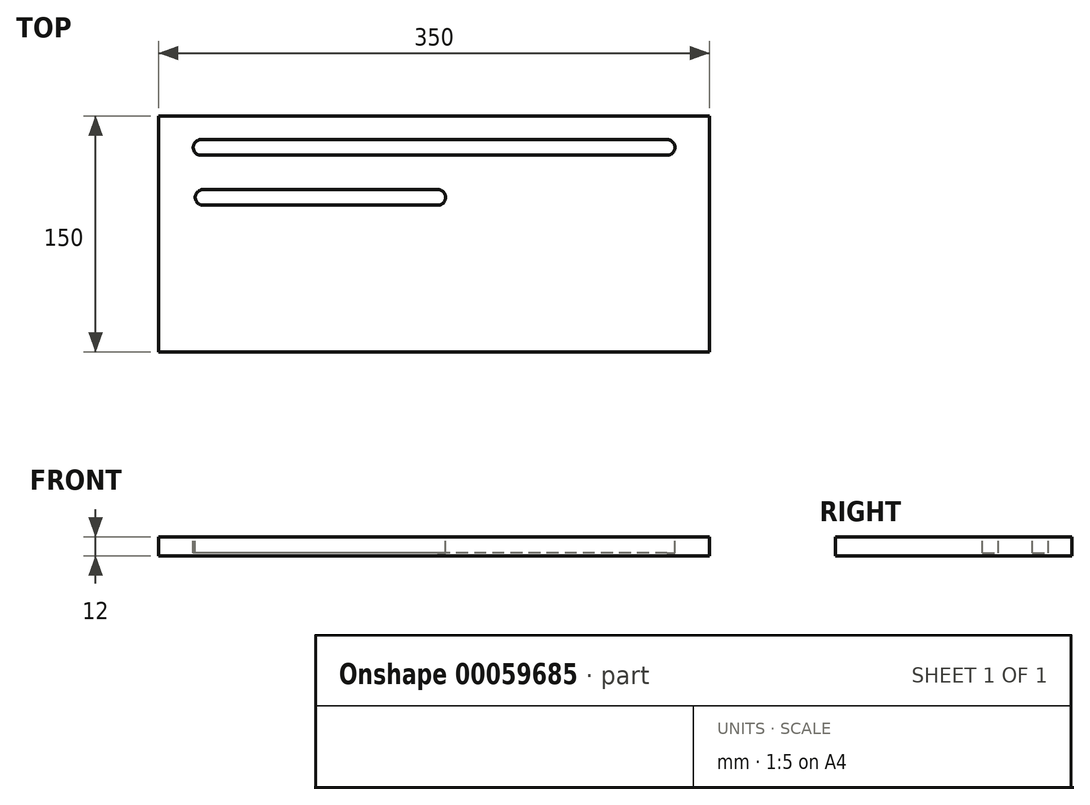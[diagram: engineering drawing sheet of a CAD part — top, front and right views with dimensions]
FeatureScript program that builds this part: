
annotation { "Feature Type Name" : "Feature", "Feature Type Description" : "" }
export const myFeature = defineFeature(function(context is Context, id is Id, definition is map)
    precondition{}
    {
        {
            var Q0;
            Q0=qCreatedBy(makeId("Top.planeOp"),FACE);
            var sketch = newSketch(context, id + "F0", { "sketchPlane" : qUnion([Q0])});
            skLineSegment(sketch, "E0.rect.bottom", {"start": v(175, 75) * mm, "end": v(-175, 75) * mm});
            skLineSegment(sketch, "E0.rect.top", {"start": v(175, -75) * mm, "end": v(-175, -75) * mm});
            skLineSegment(sketch, "E0.rect.left", {"start": v(175, 75) * mm, "end": v(175, -75) * mm});
            skLineSegment(sketch, "E0.rect.right", {"start": v(-175, 75) * mm, "end": v(-175, -75) * mm});
            skPoint(sketch, "E0.rect.middle", {"position": v(0, 0) * mm});
            skSolve(sketch);
        }
        {
            var Q0;
            Q0=makeQuery(id+"F0.imprint","IMPRINT",FACE,{"disambiguationData":[TD([[makeQuery(id+"F0.imprint","IMPRINT",EDGE,{"derivedFrom":sQuery(id+"F0.wireOp",EDGE,"E0.rect.bottom")}),1.0]])]});
            extrude(context, id + "F1", {"entities" : qUnion([Q0]), "depth" : 12 * mm});
        }
        {
            var Q0;
            Q0=makeQuery(id+"F1.opExtrude","CAP_FACE",FACE,{"disambiguationData":[OSD([sQuery(id+"F0.wireOp",EDGE,"E0.rect.bottom"),sQuery(id+"F0.wireOp",EDGE,"E0.rect.top"),sQuery(id+"F0.wireOp",EDGE,"E0.rect.left"),sQuery(id+"F0.wireOp",EDGE,"E0.rect.right")])],"isStart":false});
            var sketch = newSketch(context, id + "F2", { "sketchPlane" : qUnion([Q0])});
            skLineSegment(sketch, "E1.rect.bottom", {"start": v(153, 60) * mm, "end": v(-153, 60) * mm, "construction": true});
            skLineSegment(sketch, "E1.rect.top", {"start": v(153, 50) * mm, "end": v(-153, 50) * mm, "construction": true});
            skLineSegment(sketch, "E1.rect.left", {"start": v(153, 60) * mm, "end": v(153, 50) * mm, "construction": true});
            skLineSegment(sketch, "E1.rect.right", {"start": v(-153, 60) * mm, "end": v(-153, 50) * mm, "construction": true});
            skPoint(sketch, "E1.rect.middle", {"position": v(0, 55) * mm});
            skArc(sketch, "E2", {"start": v(-148, 60) * mm, "mid": v(-153, 55) * mm, "end": v(-148, 50) * mm});
            skArc(sketch, "E3", {"start": v(148, 50) * mm, "mid": v(153, 55) * mm, "end": v(148, 60) * mm});
            skLineSegment(sketch, "E4", {"start": v(148, 60) * mm, "end": v(-148, 60) * mm});
            skLineSegment(sketch, "E5", {"start": v(-148, 50) * mm, "end": v(148, 50) * mm});
            skLineSegment(sketch, "E6", {"start": v(2.28, 28.27) * mm, "end": v(-146.72, 28.27) * mm});
            skArc(sketch, "E7", {"start": v(2.28, 18.27) * mm, "mid": v(7.28, 23.27) * mm, "end": v(2.28, 28.27) * mm});
            skLineSegment(sketch, "E8.rect.left", {"start": v(7.28, 28.27) * mm, "end": v(7.28, 18.27) * mm, "construction": true});
            skPoint(sketch, "E8.rect.middle", {"position": v(-72.22, 23.27) * mm});
            skLineSegment(sketch, "E8.rect.bottom", {"start": v(7.28, 28.27) * mm, "end": v(-151.72, 28.27) * mm, "construction": true});
            skArc(sketch, "E9", {"start": v(-146.72, 28.27) * mm, "mid": v(-151.72, 23.27) * mm, "end": v(-146.72, 18.27) * mm});
            skLineSegment(sketch, "E8.rect.top", {"start": v(7.28, 18.27) * mm, "end": v(-151.72, 18.27) * mm, "construction": true});
            skLineSegment(sketch, "E8.rect.right", {"start": v(-151.72, 28.27) * mm, "end": v(-151.72, 18.27) * mm, "construction": true});
            skLineSegment(sketch, "E10", {"start": v(-146.72, 18.27) * mm, "end": v(2.28, 18.27) * mm});
            skSolve(sketch);
        }
        {
            var Q0;
            Q0 = qSketchRegion(id + "F2", true);
            extrude(context, id + "F3", {"entities" : qUnion([Q0]), "operationType" : NewBodyOperationType.REMOVE, "oppositeDirection" : true, "depth" : 10 * mm});
        }
    });
